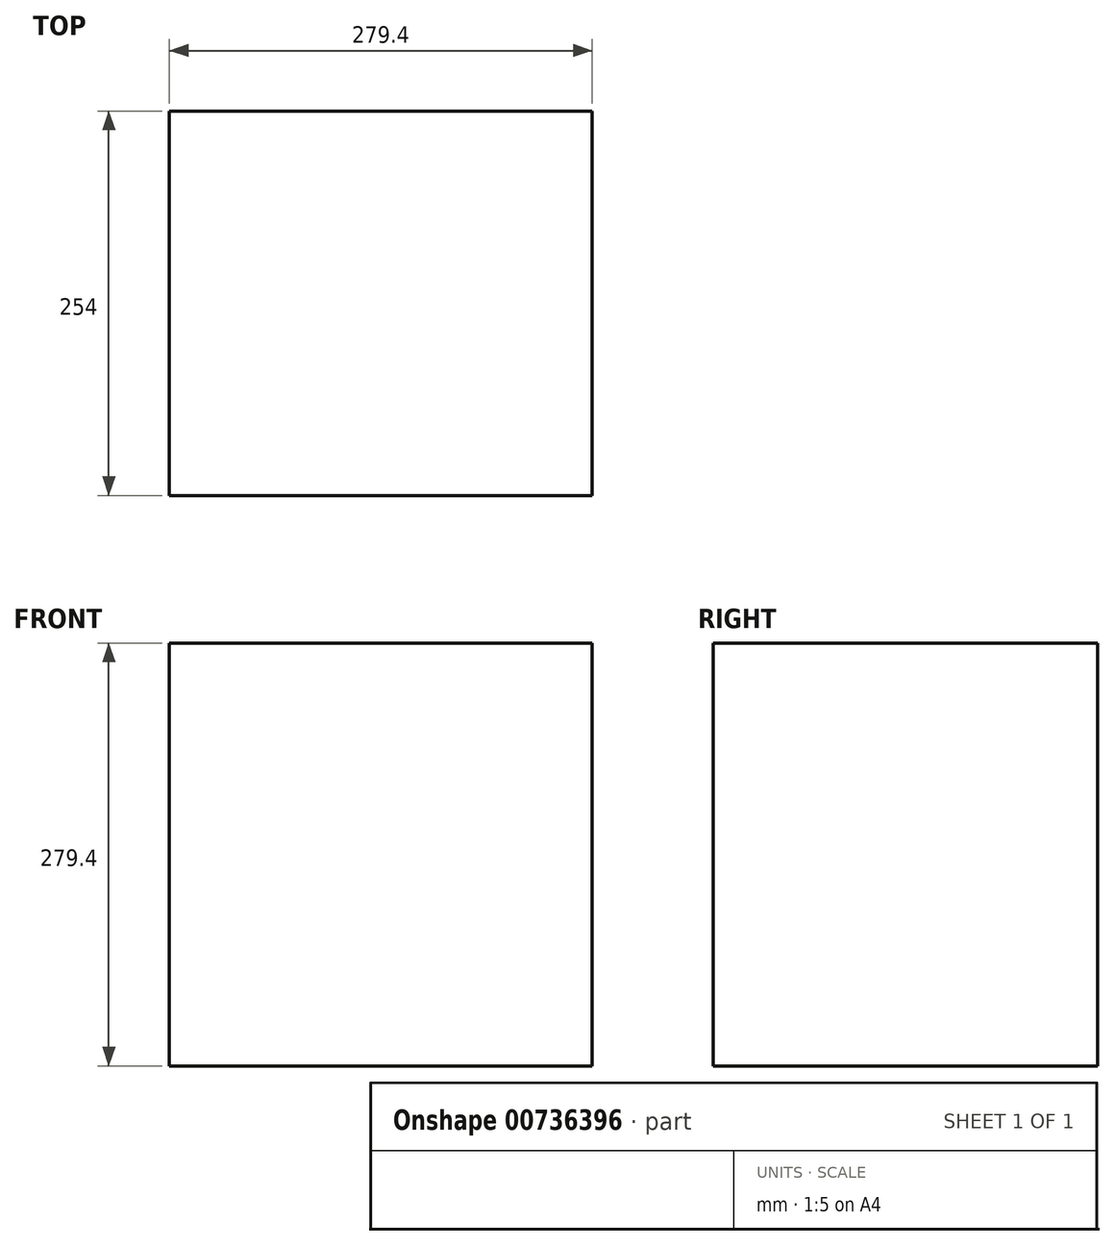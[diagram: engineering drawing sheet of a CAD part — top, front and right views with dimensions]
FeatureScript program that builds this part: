
annotation { "Feature Type Name" : "Feature", "Feature Type Description" : "" }
export const myFeature = defineFeature(function(context is Context, id is Id, definition is map)
    precondition{}
    {
        {
            var Q0;
            Q0=qCreatedBy(makeId("Front.planeOp"),FACE);
            var sketch = newSketch(context, id + "F0", { "sketchPlane" : qUnion([Q0])});
            skLineSegment(sketch, "E0.bottom", {"start": v(0, 0) * mm, "end": v(279.4, 0) * mm});
            skLineSegment(sketch, "E0.top", {"start": v(0, 279.4) * mm, "end": v(279.4, 279.4) * mm});
            skLineSegment(sketch, "E0.left", {"start": v(0, 0) * mm, "end": v(0, 279.4) * mm});
            skLineSegment(sketch, "E0.right", {"start": v(279.4, 0) * mm, "end": v(279.4, 279.4) * mm});
            skSolve(sketch);
        }
        {
            var Q0;
            Q0=makeQuery(id+"F0.imprint","IMPRINT",FACE,{"disambiguationData":[TD([[makeQuery(id+"F0.imprint","IMPRINT",EDGE,{"derivedFrom":sQuery(id+"F0.wireOp",EDGE,"E0.bottom")}),1.0]])]});
            extrude(context, id + "F1", {"entities" : qUnion([Q0]), "depth" : 254 * mm, "offsetDistance" : 25.4 * mm});
        }
    });
